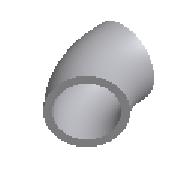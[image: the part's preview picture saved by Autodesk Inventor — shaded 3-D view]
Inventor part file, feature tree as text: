
AUTODESK INVENTOR PART (.ipt)
format: ipt  version: 2023.2 (Build 272271030, 271C)  size: 177,664 bytes
history: native  units: mm (DEFAULTED — no unit token found)
features: other x4, sketch x2, sweep x1
ambient origin geometry x8: Origin, YZ Plane, XZ Plane, XY Plane, X Axis, Y Axis, Z Axis, Center Point
bodies: Solid1 (feature_tree)
feature tree (7):
  sweep  "Sweep1"
  other  "Work Point1"
  other  "Work Point2"
  other  "Work Axis1"
  other  "Work Axis2"
  sketch  "Sketch1"  dims[d0=254.2mm d1=267.4mm]
  sketch  "Sketch2"  dims[d2=105.2mm d3=45.0deg d4=105.2mm d5=0.0mm d6=0.0mm]
